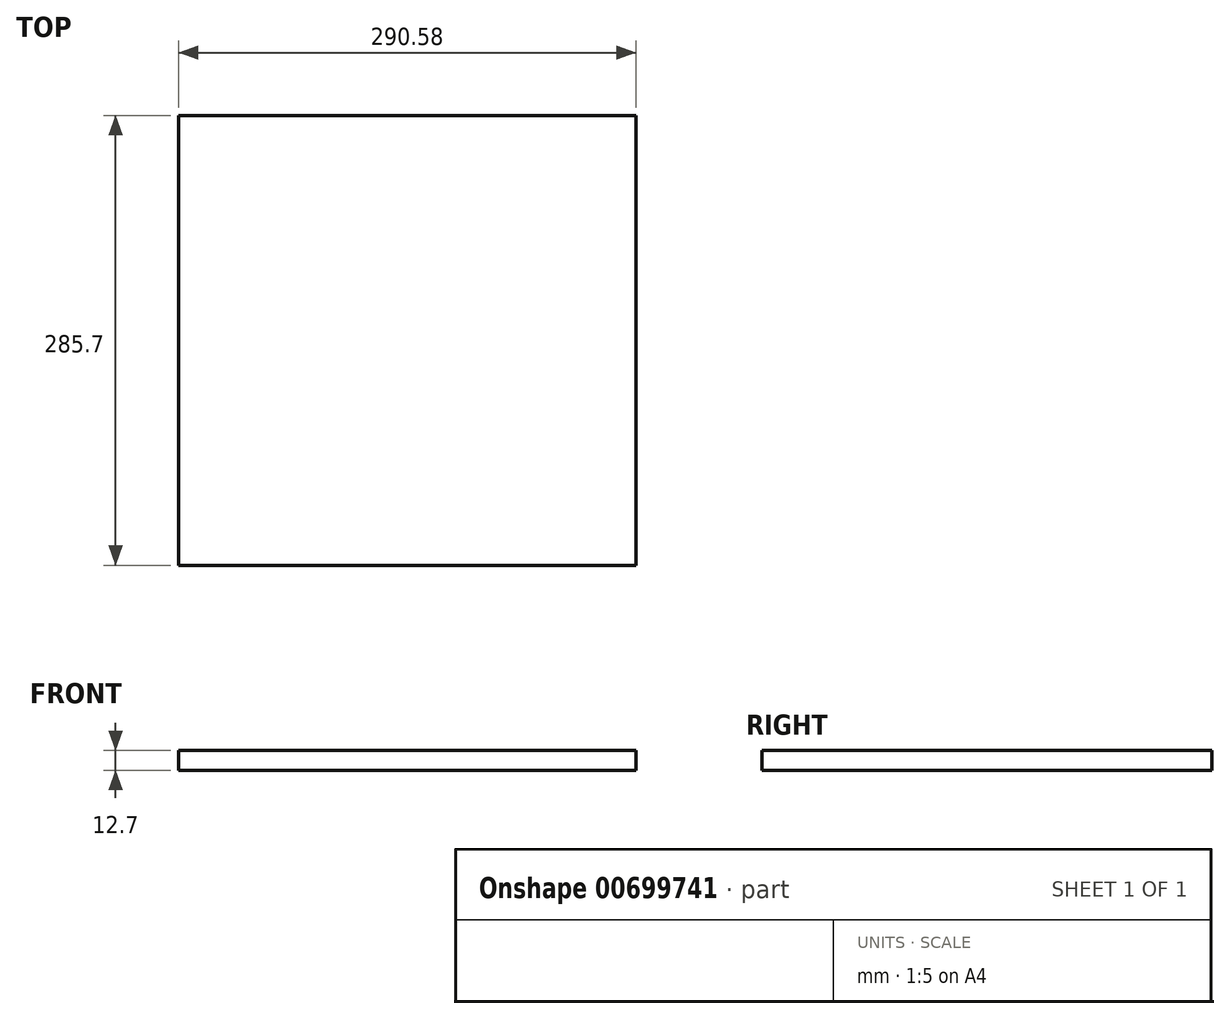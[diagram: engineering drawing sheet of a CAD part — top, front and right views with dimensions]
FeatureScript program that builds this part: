
annotation { "Feature Type Name" : "Feature", "Feature Type Description" : "" }
export const myFeature = defineFeature(function(context is Context, id is Id, definition is map)
    precondition{}
    {
        {
            var Q0;
            Q0=qCreatedBy(makeId("Top.planeOp"),FACE);
            var sketch = newSketch(context, id + "F0", { "sketchPlane" : qUnion([Q0])});
            skLineSegment(sketch, "E0.bottom", {"start": v(145.3, 142.85) * mm, "end": v(-145.3, 142.85) * mm});
            skLineSegment(sketch, "E0.top", {"start": v(145.3, -142.85) * mm, "end": v(-145.3, -142.85) * mm});
            skLineSegment(sketch, "E0.left", {"start": v(145.3, 142.85) * mm, "end": v(145.3, -142.85) * mm});
            skLineSegment(sketch, "E0.right", {"start": v(-145.3, 142.85) * mm, "end": v(-145.3, -142.85) * mm});
            skPoint(sketch, "E0.middle", {"position": v(0, 0) * mm});
            skSolve(sketch);
        }
        {
            var Q0;
            Q0=makeQuery(id+"F0.imprint","IMPRINT",FACE,{"disambiguationData":[TD([[makeQuery(id+"F0.imprint","IMPRINT",EDGE,{"derivedFrom":sQuery(id+"F0.wireOp",EDGE,"E0.bottom")}),1.0]])]});
            extrude(context, id + "F1", {"entities" : qUnion([Q0]), "depth" : 12.7 * mm, "offsetDistance" : 25.4 * mm});
        }
    });
